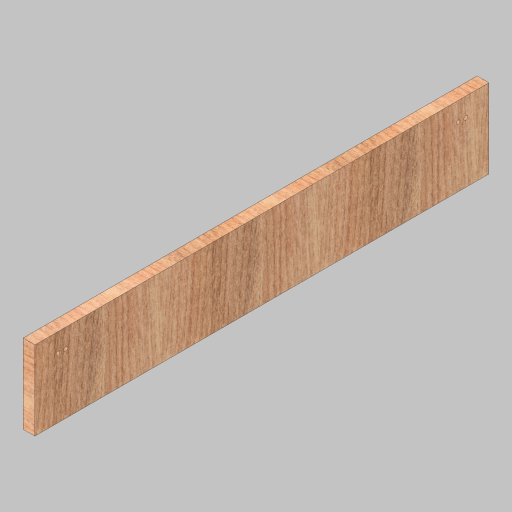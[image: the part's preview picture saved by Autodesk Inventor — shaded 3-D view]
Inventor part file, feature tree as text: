
AUTODESK INVENTOR PART (.ipt)
format: ipt  version: 2023.5 (Build 275446000, 446)  size: 229,376 bytes
history: native  units: in
note: dims shown in document units (in); Inventor stores cm internally (conversion verified against a paired STEP export)
features: sketch x2, extrude x1, hole x1
ambient origin geometry x8: Origin, YZ Plane, XZ Plane, XY Plane, X Axis, Y Axis, Z Axis, Center Point
bodies: Solid1 (feature_tree)
feature tree (4):
  extrude  "Extrusion1"  Depth=28.75in
  hole  "Hole1"  [1 undecoded]
  sketch  "Sketch1"  dims[d0=5.0in d1=28.75in]
  sketch  "Sketch2"  dims[d2=0.75in d3=0.0in d4=1.461in d5=0.5in d6=1.188in d7=0.25in d8=0.75in d9=0.385in d10=0.25in d11=0.5635in d12=1.0in d13=0.8108in]
note: 1 required parameter value undecoded (feature->parameter linkage not recoverable at this tier; creation-order binding heuristic only, values carry confidence <= 0.55)
